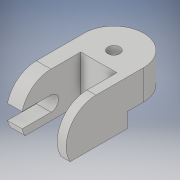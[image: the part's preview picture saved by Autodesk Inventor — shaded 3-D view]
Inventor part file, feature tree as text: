
AUTODESK INVENTOR PART (.ipt)
format: ipt  version: 2018 (Build 220112000, 112)  size: 183,296 bytes
history: native  units: in
note: dims shown in document units (in); Inventor stores cm internally (conversion verified against a paired STEP export)
features: sketch x10, extrude x9
ambient origin geometry x8: Origin, YZ Plane, XZ Plane, XY Plane, X Axis, Y Axis, Z Axis, Center Point
bodies: Solid1 (feature_tree)
feature tree (19):
  sketch  "Sketch1"  dims[d1=0.1181in d5=0.7874in d6=0.0in]
  extrude  "Extrusion1"  Depth=0.7874in TaperAngle=0.0deg
  extrude  "Extrusion2"  Depth=0.1929in
  extrude  "Extrusion3"  Depth=0.4764in
  extrude  "Extrusion4"  Depth=0.1969in
  extrude  "Extrusion5"  Depth=0.1969in
  extrude  "Extrusion6"  Depth=0.1575in
  extrude  "Extrusion7"  Depth=0.3543in
  extrude  "Extrusion8"  Depth=0.1575in TaperAngle=0.0deg
  extrude  "Extrusion9"  Depth=0.4331in
  sketch  "Sketch2"  dims[d7=0.7874in d8=0.0in d10=0.1929in]
  sketch  "Sketch3"  dims[d11=0.7874in d12=0.4764in]
  sketch  "Sketch5"  dims[d13=0.7874in d14=0.0in d15=0.1969in]
  sketch  "Sketch6"  dims[d16=0.1969in d17=0.0in d18=0.1969in]
  sketch  "Sketch7"  dims[d19=0.7874in d20=0.0in d21=0.1575in]
  sketch  "Sketch8"  dims[d22=0.7874in d23=0.0in d24=0.3543in]
  sketch  "Sketch9"  dims[d25=0.3937in d26=0.0in d31=0.1575in d32=0.0in]
  sketch  "Sketch12"  dims[d33=0.4331in d34=0.4331in]
  sketch  "Sketch13"  dims[d35=0.1969in d36=0.0in]
